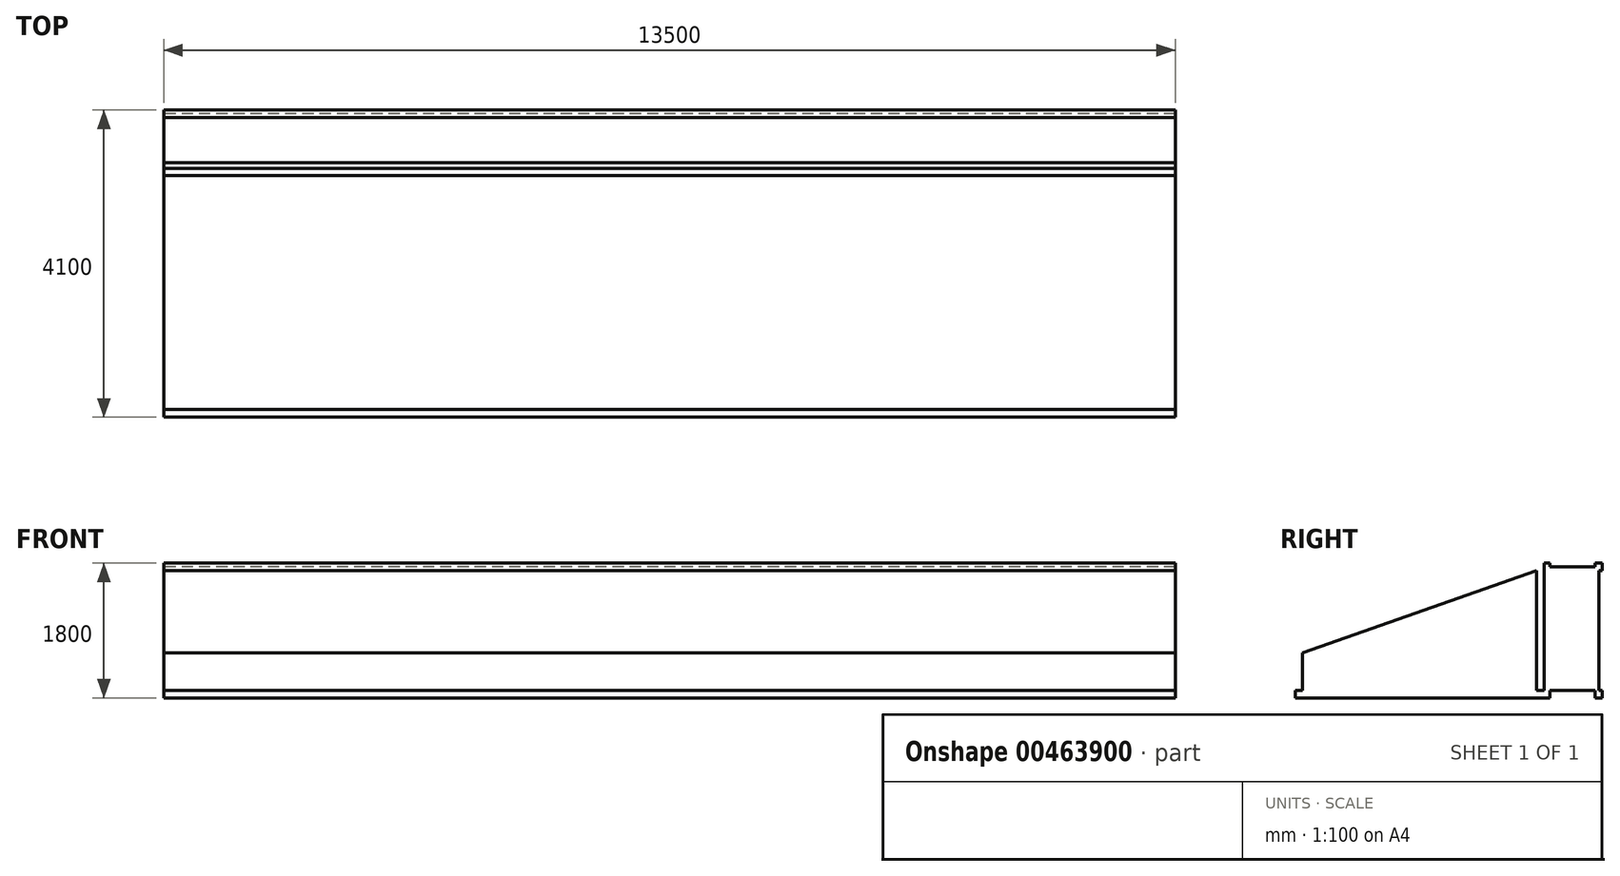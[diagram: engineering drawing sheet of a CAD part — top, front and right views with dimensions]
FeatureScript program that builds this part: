
annotation { "Feature Type Name" : "Feature", "Feature Type Description" : "" }
export const myFeature = defineFeature(function(context is Context, id is Id, definition is map)
    precondition{}
    {
        {
            var Q0;
            Q0=qCreatedBy(makeId("Right.planeOp"),FACE);
            var sketch = newSketch(context, id + "F0", { "sketchPlane" : qUnion([Q0])});
            skLineSegment(sketch, "E0", {"start": v(0, 0) * mm, "end": v(-100, 0) * mm});
            skLineSegment(sketch, "E1", {"start": v(-100, 0) * mm, "end": v(-100, 100) * mm});
            skLineSegment(sketch, "E2", {"start": v(-100, 100) * mm, "end": v(-700, 100) * mm});
            skLineSegment(sketch, "E3", {"start": v(-700, 100) * mm, "end": v(-700, 0) * mm});
            skLineSegment(sketch, "E4", {"start": v(-700, 0) * mm, "end": v(-800, 0) * mm});
            skLineSegment(sketch, "E5", {"start": v(-900, 0) * mm, "end": v(-4100, 0) * mm});
            skPoint(sketch, "E5.endSnap0", {"position": v(-750, 0) * mm});
            skLineSegment(sketch, "E6", {"start": v(-4100, 0) * mm, "end": v(-4100, 100) * mm});
            skLineSegment(sketch, "E7", {"start": v(-4100, 100) * mm, "end": v(-4000, 100) * mm});
            skLineSegment(sketch, "E8", {"start": v(-4000, 100) * mm, "end": v(-4000, 600) * mm});
            skLineSegment(sketch, "E9", {"start": v(0, 0) * mm, "end": v(0, 100) * mm});
            skLineSegment(sketch, "E10", {"start": v(0, 100) * mm, "end": v(-50, 100) * mm});
            skLineSegment(sketch, "E11", {"start": v(-100, 1750) * mm, "end": v(-700, 1750) * mm});
            skLineSegment(sketch, "E12", {"start": v(-700, 1750) * mm, "end": v(-700, 1800) * mm});
            skLineSegment(sketch, "E13", {"start": v(-700, 1800) * mm, "end": v(-776.63, 1800) * mm});
            skLineSegment(sketch, "E14", {"start": v(-776.63, 1800) * mm, "end": v(-776.63, 1750) * mm});
            skLineSegment(sketch, "E15", {"start": v(-50, 100) * mm, "end": v(-50, 1700) * mm});
            skLineSegment(sketch, "E16", {"start": v(-50, 1700) * mm, "end": v(0, 1700) * mm});
            skLineSegment(sketch, "E17", {"start": v(0, 1700) * mm, "end": v(0, 1800) * mm});
            skLineSegment(sketch, "E18", {"start": v(0, 1800) * mm, "end": v(-100, 1800) * mm});
            skLineSegment(sketch, "E19", {"start": v(-100, 1800) * mm, "end": v(-100, 1750) * mm});
            skLineSegment(sketch, "E20", {"start": v(-776.63, 1750) * mm, "end": v(-776.63, 100) * mm});
            skLineSegment(sketch, "E21", {"start": v(-800, 0) * mm, "end": v(-900, 0) * mm});
            skLineSegment(sketch, "E22", {"start": v(-876.63, 100) * mm, "end": v(-876.63, 1700) * mm});
            skLineSegment(sketch, "E23", {"start": v(-876.63, 1700) * mm, "end": v(-4000, 600) * mm});
            skLineSegment(sketch, "E24", {"start": v(-876.63, 100) * mm, "end": v(-776.63, 100) * mm});
            skSolve(sketch);
        }
        {
            var Q0;
            Q0=makeQuery(id+"F0.imprint","IMPRINT",FACE,{"disambiguationData":[TD([[makeQuery(id+"F0.imprint","IMPRINT",EDGE,{"derivedFrom":sQuery(id+"F0.wireOp",EDGE,"E0")}),-1.0]])]});
            extrude(context, id + "F1", {"entities" : qUnion([Q0]), "depth" : 13500 * mm});
        }
    });
